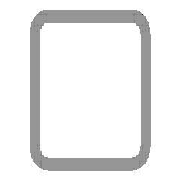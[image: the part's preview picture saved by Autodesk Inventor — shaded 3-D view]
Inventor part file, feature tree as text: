
AUTODESK INVENTOR PART (.ipt)
format: ipt  version: 2021 (Build 250183000, 183)  size: 130,048 bytes
history: native  units: mm (DEFAULTED — no unit token found)
features: other x4, sketch x3, extrude x1, plane x1
ambient origin geometry x8: Origin, YZ Plane, XZ Plane, XY Plane, X Axis, Y Axis, Z Axis, Center Point
bodies: Solid1 (feature_tree)
feature tree (9):
  parser-record x1  (decoder bookkeeping rows leaked as tree rows — omitted from the tree; the rows remain in map.json)
  other  "Driven Length"
  other  "Plano inicial"
  other  "Plano final"
  extrude  "Corpo"  TaperAngle=0.0deg  [1 undecoded]
  sketch  "Esboço"  dims[d11=50.8mm d12=4.7625mm d13=-0.0mm d14=4000.0mm d15=25.4mm d16=25.4mm d17=9.525mm d18=90.0deg d19=4000.0mm]
  sketch  "Sketch3"  dims[d3=4000.0mm d4=0.0mm]
  plane  "Work Plane3"
  sketch  "Sketch4"  dims[d10=50.8mm]
note: 1 required parameter value undecoded (feature->parameter linkage not recoverable at this tier; creation-order binding heuristic only, values carry confidence <= 0.55)
